# Revit family: JN
name_source: partatom
category: Air Terminals
revit_build: Autodesk Revit MEP 2012 (Build: 20110309_2315(x64)
units: mm (PartAtom-declared; Revit-internal decimal feet)

## types (4) — shared parameters
Manufacturer = INNES
Máxima presión estática = 0.00 in-wg
Máxima velocidad de cuello = 0 FPM
Mínima presión estática = 0.00 in-wg
Mínima velocidad de cuello = 0 FPM
URL = http://www.innes.com.mx

## per-type parameters (varying)
| type | A | A1 | B | C | C1 | C2 | D | D1 | D2 | D3 |
| JN-160 | 158 mm  [stored 0.518373 ft] | 163 mm | 216 mm  [stored 0.708661 ft] | 82 mm  [stored 0.269029 ft] | 102 mm  [stored 0.334646 ft] | 132 mm  [stored 0.433071 ft] | 106 mm  [stored 0.347769 ft] | 6 mm | 30 mm  [stored 0.0984252 ft] | 10 mm  [stored 0.0328084 ft] |
| JN-200 | 198 mm  [stored 0.649606 ft] | 203 mm  [stored 0.66601 ft] | 273 mm  [stored 0.895669 ft] | 108 mm  [stored 0.354331 ft] | 128 mm  [stored 0.419948 ft] | 158 mm  [stored 0.518373 ft] | 127 mm | 7 mm | 36 mm  [stored 0.11811 ft] | 12 mm  [stored 0.0393701 ft] |
| JN-250 | 248 mm  [stored 0.813648 ft] | 253 mm  [stored 0.830052 ft] | 318 mm  [stored 1.04331 ft] | 136 mm | 156 mm  [stored 0.511811 ft] | 186 mm  [stored 0.610236 ft] | 159 mm  [stored 0.521654 ft] | 9 mm | 45 mm | 15 mm |
| JN-315 | 313 mm  [stored 1.0269 ft] | 318 mm  [stored 1.04331 ft] | 400 mm  [stored 1.31234 ft] | 174 mm  [stored 0.570866 ft] | 194 mm  [stored 0.636483 ft] | 224 mm | 189 mm  [stored 0.620079 ft] | 11 mm | 54 mm  [stored 0.177165 ft] | 18 mm  [stored 0.0590551 ft] |

note: [stored X ft] marks values corroborated as IEEE doubles in the binary element streams (Revit-internal decimal feet)

## geometry (parser evidence)
native form markers: Sweep x1
no freeform markers — native parametric forms only
